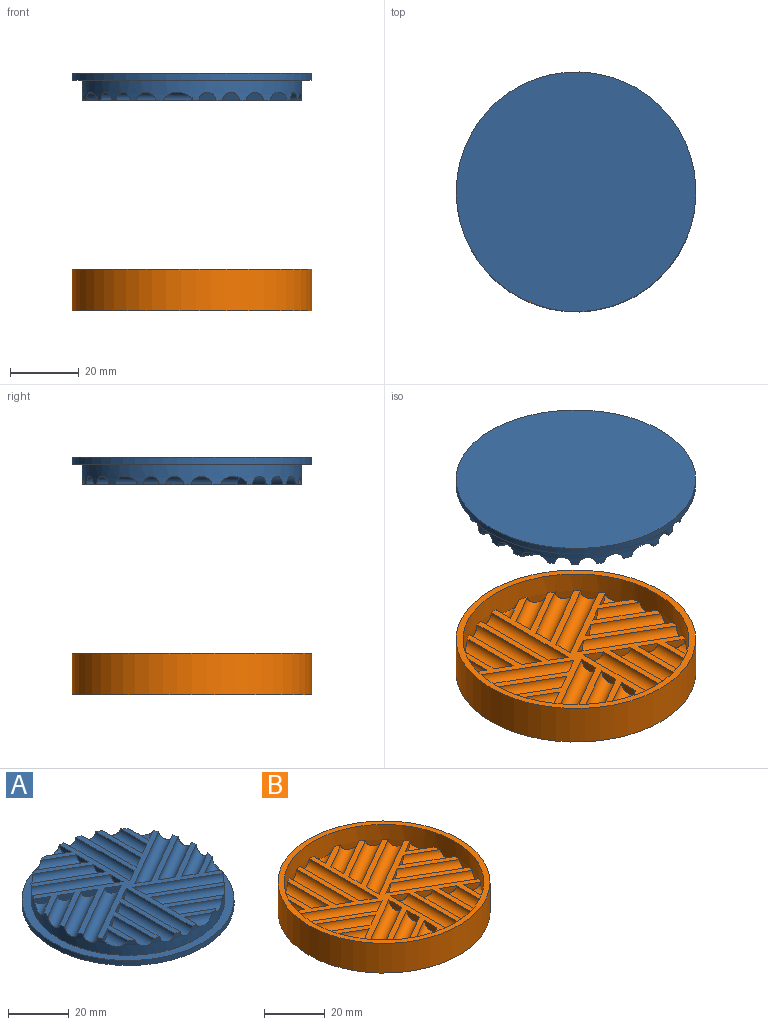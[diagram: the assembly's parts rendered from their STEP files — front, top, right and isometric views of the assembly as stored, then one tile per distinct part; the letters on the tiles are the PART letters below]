
ASSEMBLY  parts=2 mates=1
PART A: 53 faces, bbox 70x70.5x8 mm
  f0: plane 5.69x2.46mm, normal (-1,0,0), area 11mm2, adj f5,f47
  f1: plane 5.69x2.46mm, normal (-1,0,0), area 11mm2, adj f5,f48
  f2: plane 5.69x2.46mm, normal (-1,0,0), area 11mm2, adj f5,f46
  f3: plane 5.69x2.46mm, normal (-1,0,0), area 11mm2, adj f5,f49
  f4: cylinder r=32mm len=64mm, axis (0,0,-1), area 922.8mm2, adj f5,f6,f7,f8,f9,f14,f15,f16
  f5: plane 64x64mm, normal (0,0,1), area 1061.1mm2, adj f0,f1,f2,f3,f4,f6,f7,f8
  f6: cylinder r=2.46mm len=25.57mm, axis (0,1,0), area 180.1mm2, adj f4,f5,f13
  f7: cylinder r=2.46mm len=9.31mm, axis (0,1,0), area 37.7mm2, adj f4,f5,f11
  f8: cylinder r=2.46mm len=18.64mm, axis (0,1,0), area 120.6mm2, adj f4,f5,f12
  f9: cylinder r=2.46mm len=30.78mm, axis (0,1,0), area 225mm2, adj f4,f5,f10
  f10: plane 4.93x2.85mm, normal (-0.5,0.87,0), area 11mm2, adj f5,f9
  f11: plane 4.93x2.85mm, normal (-0.5,0.87,0), area 11mm2, adj f5,f7
  f12: plane 4.93x2.85mm, normal (-0.5,0.87,0), area 11mm2, adj f5,f8
  f13: plane 4.93x2.85mm, normal (-0.5,0.87,0), area 11mm2, adj f5,f6
  f14: cylinder r=2.46mm len=24.61mm, axis (0.87,0.5,0), area 180.1mm2, adj f4,f5,f21
  f15: cylinder r=2.46mm len=10.53mm, axis (0.87,0.5,0), area 37.7mm2, adj f4,f5,f19
  f16: cylinder r=2.46mm len=18.61mm, axis (0.87,0.5,0), area 120.6mm2, adj f4,f5,f20
  f17: cylinder r=2.46mm len=29.12mm, axis (0.87,0.5,0), area 225mm2, adj f4,f5,f18
  f18: plane 4.93x2.85mm, normal (0.5,0.87,0), area 11mm2, adj f5,f17
  f19: plane 4.93x2.85mm, normal (0.5,0.87,0), area 11mm2, adj f5,f15
  f20: plane 4.93x2.85mm, normal (0.5,0.87,0), area 11mm2, adj f5,f16
  f21: plane 4.93x2.85mm, normal (0.5,0.87,0), area 11mm2, adj f5,f14
  f22: cylinder r=2.46mm len=24.61mm, axis (0.87,-0.5,0), area 180.1mm2, adj f4,f5,f29
  f23: cylinder r=2.46mm len=10.53mm, axis (0.87,-0.5,0), area 37.7mm2, adj f4,f5,f27
  f24: cylinder r=2.46mm len=18.61mm, axis (0.87,-0.5,0), area 120.6mm2, adj f4,f5,f28
  f25: cylinder r=2.46mm len=29.12mm, axis (0.87,-0.5,0), area 225mm2, adj f4,f5,f26
  f26: plane 5.69x2.46mm, normal (1,0,0), area 11mm2, adj f5,f25
  f27: plane 5.69x2.46mm, normal (1,0,0), area 11mm2, adj f5,f23
  f28: plane 5.69x2.46mm, normal (1,0,0), area 11mm2, adj f5,f24
  f29: plane 5.69x2.46mm, normal (1,0,0), area 11mm2, adj f5,f22
  f30: cylinder r=2.46mm len=25.57mm, axis (0,-1,0), area 180.1mm2, adj f4,f5,f37
  f31: cylinder r=2.46mm len=9.31mm, axis (0,-1,0), area 37.7mm2, adj f4,f5,f35
  f32: cylinder r=2.46mm len=18.64mm, axis (0,-1,0), area 120.6mm2, adj f4,f5,f36
  f33: cylinder r=2.46mm len=30.78mm, axis (0,-1,0), area 225mm2, adj f4,f5,f34
  f34: plane 4.93x2.85mm, normal (0.5,-0.87,0), area 11mm2, adj f5,f33
  f35: plane 4.93x2.85mm, normal (0.5,-0.87,0), area 11mm2, adj f5,f31
  f36: plane 4.93x2.85mm, normal (0.5,-0.87,0), area 11mm2, adj f5,f32
  f37: plane 4.93x2.85mm, normal (0.5,-0.87,0), area 11mm2, adj f5,f30
  f38: cylinder r=2.46mm len=24.61mm, axis (-0.87,-0.5,0), area 180.1mm2, adj f4,f5,f45
  f39: cylinder r=2.46mm len=10.53mm, axis (-0.87,-0.5,0), area 37.7mm2, adj f4,f5,f43
  f40: cylinder r=2.46mm len=18.61mm, axis (-0.87,-0.5,0), area 120.6mm2, adj f4,f5,f44
  f41: cylinder r=2.46mm len=29.12mm, axis (-0.87,-0.5,0), area 225mm2, adj f4,f5,f42
  f42: plane 4.93x2.85mm, normal (-0.5,-0.87,0), area 11mm2, adj f5,f41
  f43: plane 4.93x2.85mm, normal (-0.5,-0.87,0), area 11mm2, adj f5,f39
  f44: plane 4.93x2.85mm, normal (-0.5,-0.87,0), area 11mm2, adj f5,f40
  f45: plane 4.93x2.85mm, normal (-0.5,-0.87,0), area 11mm2, adj f5,f38
  f46: cylinder r=2.46mm len=24.61mm, axis (-0.87,0.5,0), area 180.1mm2, adj f2,f4,f5
  f47: cylinder r=2.46mm len=10.53mm, axis (-0.87,0.5,0), area 37.7mm2, adj f0,f4,f5
  f48: cylinder r=2.46mm len=18.61mm, axis (-0.87,0.5,0), area 120.6mm2, adj f1,f4,f5
  f49: cylinder r=2.46mm len=29.12mm, axis (-0.87,0.5,0), area 225mm2, adj f3,f4,f5
  f50: cylinder r=35mm len=70mm, axis (0,0,1), area 439.8mm2, adj f51,f52
  f51: plane 70x70mm, normal (0,0,-1), area 3848.5mm2, adj f50
  f52: plane 70x70mm, normal (0,0,1), area 631.5mm2, adj f4,f50
PART B: 53 faces, bbox 71.1x72.7x12 mm
  f0: plane 5.94x2.57mm, normal (1,0,0), area 12mm2, adj f4,f20
  f1: plane 5.94x2.57mm, normal (1,0,0), area 12mm2, adj f4,f19
  f2: plane 5.94x2.57mm, normal (1,0,0), area 12mm2, adj f4,f18
  f3: plane 5.94x2.57mm, normal (1,0,0), area 12mm2, adj f4,f17
  f4: plane 66x66mm, normal (0,0,1), area 1095.8mm2, adj f0,f1,f2,f3,f5,f6,f7,f8
  f5: cylinder r=2.57mm len=9.71mm, axis (0,1,0), area 41mm2, adj f4,f12,f49
  f6: cylinder r=2.57mm len=19.29mm, axis (0,1,0), area 130.1mm2, adj f4,f11,f49
  f7: cylinder r=2.57mm len=26.43mm, axis (0,1,0), area 194.1mm2, adj f4,f10,f49
  f8: cylinder r=2.57mm len=31.78mm, axis (0,1,0), area 242.4mm2, adj f4,f9,f49
  f9: plane 5.14x2.97mm, normal (0.5,0.87,0), area 12mm2, adj f4,f8
  f10: plane 5.14x2.97mm, normal (0.5,0.87,0), area 12mm2, adj f4,f7
  f11: plane 5.14x2.97mm, normal (0.5,0.87,0), area 12mm2, adj f4,f6
  f12: plane 5.14x2.97mm, normal (0.5,0.87,0), area 12mm2, adj f4,f5
  f13: plane 5.14x2.97mm, normal (0.5,-0.87,0), area 12mm2, adj f4,f28
  f14: plane 5.14x2.97mm, normal (0.5,-0.87,0), area 12mm2, adj f4,f27
  f15: plane 5.14x2.97mm, normal (0.5,-0.87,0), area 12mm2, adj f4,f26
  f16: plane 5.14x2.97mm, normal (0.5,-0.87,0), area 12mm2, adj f4,f25
  f17: cylinder r=2.57mm len=10.98mm, axis (0.87,0.5,0), area 41mm2, adj f3,f4,f49
  f18: cylinder r=2.57mm len=19.28mm, axis (0.87,0.5,0), area 130.1mm2, adj f2,f4,f49
  f19: cylinder r=2.57mm len=25.46mm, axis (0.87,0.5,0), area 194.1mm2, adj f1,f4,f49
  f20: cylinder r=2.57mm len=30.1mm, axis (0.87,0.5,0), area 242.4mm2, adj f0,f4,f49
  f21: plane 5.14x2.97mm, normal (-0.5,-0.87,0), area 12mm2, adj f4,f36
  f22: plane 5.14x2.97mm, normal (-0.5,-0.87,0), area 12mm2, adj f4,f35
  f23: plane 5.14x2.97mm, normal (-0.5,-0.87,0), area 12mm2, adj f4,f34
  f24: plane 5.14x2.97mm, normal (-0.5,-0.87,0), area 12mm2, adj f4,f33
  f25: cylinder r=2.57mm len=10.98mm, axis (0.87,-0.5,0), area 41mm2, adj f4,f16,f49
  f26: cylinder r=2.57mm len=19.28mm, axis (0.87,-0.5,0), area 130.1mm2, adj f4,f15,f49
  f27: cylinder r=2.57mm len=25.46mm, axis (0.87,-0.5,0), area 194.1mm2, adj f4,f14,f49
  f28: cylinder r=2.57mm len=30.1mm, axis (0.87,-0.5,0), area 242.4mm2, adj f4,f13,f49
  f29: plane 5.94x2.57mm, normal (-1,0,0), area 12mm2, adj f4,f44
  f30: plane 5.94x2.57mm, normal (-1,0,0), area 12mm2, adj f4,f43
  f31: plane 5.94x2.57mm, normal (-1,0,0), area 12mm2, adj f4,f42
  f32: plane 5.94x2.57mm, normal (-1,0,0), area 12mm2, adj f4,f41
  f33: cylinder r=2.57mm len=9.71mm, axis (0,-1,0), area 41mm2, adj f4,f24,f49
  f34: cylinder r=2.57mm len=19.29mm, axis (0,-1,0), area 130.1mm2, adj f4,f23,f49
  f35: cylinder r=2.57mm len=26.43mm, axis (0,-1,0), area 194.1mm2, adj f4,f22,f49
  f36: cylinder r=2.57mm len=31.78mm, axis (0,-1,0), area 242.4mm2, adj f4,f21,f49
  f37: plane 5.14x2.97mm, normal (-0.5,0.87,0), area 12mm2, adj f4,f48
  f38: plane 5.14x2.97mm, normal (-0.5,0.87,0), area 12mm2, adj f4,f47
  f39: plane 5.14x2.97mm, normal (-0.5,0.87,0), area 12mm2, adj f4,f46
  f40: plane 5.14x2.97mm, normal (-0.5,0.87,0), area 12mm2, adj f4,f45
  f41: cylinder r=2.57mm len=10.98mm, axis (-0.87,-0.5,0), area 41mm2, adj f4,f32,f49
  f42: cylinder r=2.57mm len=19.28mm, axis (-0.87,-0.5,0), area 130.1mm2, adj f4,f31,f49
  f43: cylinder r=2.57mm len=25.46mm, axis (-0.87,-0.5,0), area 194.1mm2, adj f4,f30,f49
  f44: cylinder r=2.57mm len=30.1mm, axis (-0.87,-0.5,0), area 242.4mm2, adj f4,f29,f49
  f45: cylinder r=2.57mm len=10.98mm, axis (-0.87,0.5,0), area 41mm2, adj f4,f40,f49
  f46: cylinder r=2.57mm len=19.28mm, axis (-0.87,0.5,0), area 130.1mm2, adj f4,f39,f49
  f47: cylinder r=2.57mm len=25.46mm, axis (-0.87,0.5,0), area 194.1mm2, adj f4,f38,f49
  f48: cylinder r=2.57mm len=30.1mm, axis (-0.87,0.5,0), area 242.4mm2, adj f4,f37,f49
  f49: cylinder r=33mm len=66mm, axis (0,0,-1), area 1553.1mm2, adj f4,f5,f6,f7,f8,f17,f18,f19
  f50: cylinder r=35mm len=70mm, axis (0,0,-1), area 2638.9mm2, adj f51,f52
  f51: plane 70x70mm, normal (0,0,1), area 427.3mm2, adj f49,f50
  f52: plane 70x70mm, normal (0,0,-1), area 3848.5mm2, adj f50
PLACE A rot(axis=(1,0,0),180deg) t=(0,0,67.24)mm
PLACE B at identity
MATE slider A.f50 <-> B.f50  axis (0,0,-1) through (0,0,67.24)mm
